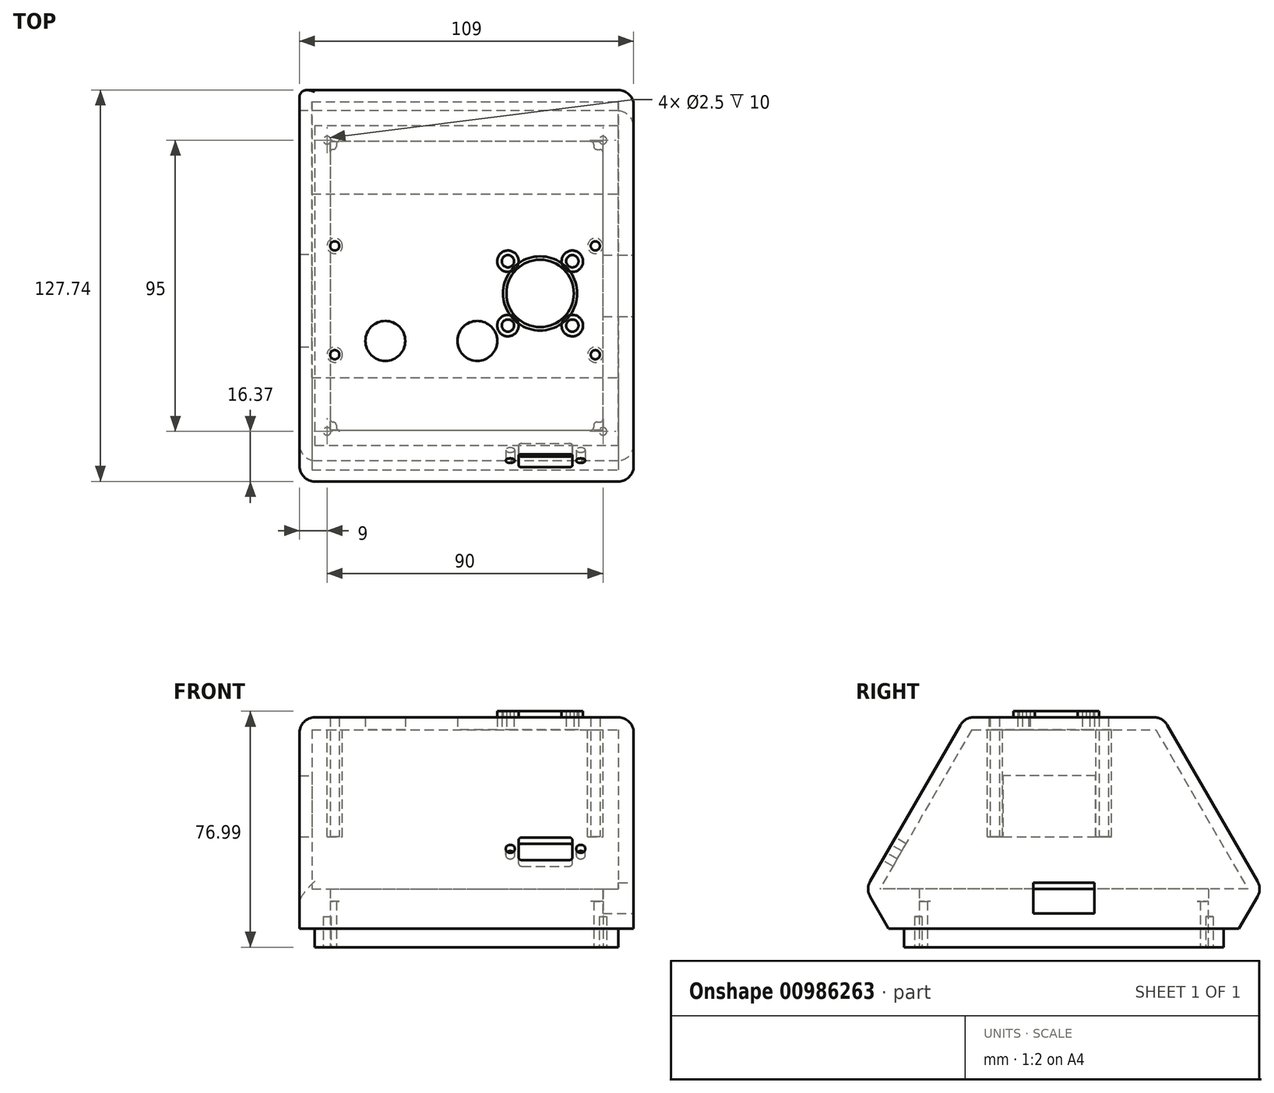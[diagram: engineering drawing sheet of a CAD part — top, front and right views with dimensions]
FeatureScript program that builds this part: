
annotation { "Feature Type Name" : "Feature", "Feature Type Description" : "" }
export const myFeature = defineFeature(function(context is Context, id is Id, definition is map)
    precondition{}
    {
        {
            var Q0;
            Q0=qCreatedBy(makeId("Top.planeOp"),FACE);
            var sketch = newSketch(context, id + "F0", { "sketchPlane" : qUnion([Q0])});
            skLineSegment(sketch, "E0.bottom", {"start": v(-50, -30) * mm, "end": v(50, -30) * mm});
            skLineSegment(sketch, "E0.top", {"start": v(-50, 30) * mm, "end": v(50, 30) * mm});
            skLineSegment(sketch, "E0.left", {"start": v(-50, -30) * mm, "end": v(-50, 30) * mm});
            skLineSegment(sketch, "E0.right", {"start": v(50, -30) * mm, "end": v(50, 30) * mm});
            skPoint(sketch, "E0.middle", {"position": v(0, 0) * mm});
            skLineSegment(sketch, "E1.bottom", {"start": v(0, -30) * mm, "end": v(0, -30) * mm});
            skLineSegment(sketch, "E1.top", {"start": v(0, 90) * mm, "end": v(0, 90) * mm});
            skLineSegment(sketch, "E1.left", {"start": v(0, -30) * mm, "end": v(0, 90) * mm, "construction": true});
            skLineSegment(sketch, "E1.right", {"start": v(0, -30) * mm, "end": v(0, 90) * mm, "construction": true});
            skPoint(sketch, "E1.middle", {"position": v(0, 30) * mm});
            skCircle(sketch, "E2", {"center": v(42.5, -22.5) * mm, "radius": 1.5 * mm});
            skCircle(sketch, "E3", {"center": v(42.5, 13) * mm, "radius": 1.5 * mm});
            skCircle(sketch, "E4.MirrorC", {"center": v(-42.5, 13) * mm, "radius": 1.5 * mm});
            skCircle(sketch, "E5.MirrorC", {"center": v(-42.5, -22.5) * mm, "radius": 1.5 * mm});
            skLineSegment(sketch, "E6.bottom", {"start": v(35, -13) * mm, "end": v(14, -13) * mm, "construction": true});
            skLineSegment(sketch, "E6.top", {"start": v(35, 8) * mm, "end": v(14, 8) * mm, "construction": true});
            skLineSegment(sketch, "E6.left", {"start": v(35, -13) * mm, "end": v(35, 8) * mm, "construction": true});
            skLineSegment(sketch, "E6.right", {"start": v(14, -13) * mm, "end": v(14, 8) * mm, "construction": true});
            skPoint(sketch, "E6.middle", {"position": v(24.5, -2.5) * mm});
            skCircle(sketch, "E7", {"center": v(14, 8) * mm, "radius": 2 * mm});
            skCircle(sketch, "E8", {"center": v(35, 8) * mm, "radius": 2 * mm});
            skCircle(sketch, "E9", {"center": v(14, -13) * mm, "radius": 2 * mm});
            skCircle(sketch, "E10", {"center": v(35, -13) * mm, "radius": 2 * mm});
            skCircle(sketch, "E11", {"center": v(24.5, -2.5) * mm, "radius": 11 * mm});
            skCircle(sketch, "E12", {"center": v(4, -18) * mm, "radius": 6.5 * mm});
            skCircle(sketch, "E13", {"center": v(-26, -18) * mm, "radius": 6.5 * mm});
            skSolve(sketch);
        }
        {
            var Q0;
            Q0=makeQuery(id+"F0.imprint","IMPRINT",FACE,{"disambiguationData":[TD([[makeQuery(id+"F0.imprint","IMPRINT",EDGE,{"derivedFrom":sQuery(id+"F0.wireOp",EDGE,"E0.bottom")}),1.0]])]});
            extrude(context, id + "F1", {"entities" : qUnion([Q0]), "depth" : 4 * mm, "offsetDistance" : 25 * mm});
        }
        {
            var Q0;
            Q0=makeQuery(id+"F1.opExtrude","CAP_FACE",FACE,{"disambiguationData":[OSD([sQuery(id+"F0.wireOp",EDGE,"E0.bottom"),sQuery(id+"F0.wireOp",EDGE,"E0.top"),sQuery(id+"F0.wireOp",EDGE,"E0.left"),sQuery(id+"F0.wireOp",EDGE,"E0.right"),sQuery(id+"F0.wireOp",EDGE,"E2"),sQuery(id+"F0.wireOp",EDGE,"E3"),sQuery(id+"F0.wireOp",EDGE,"E4.MirrorC"),sQuery(id+"F0.wireOp",EDGE,"E5.MirrorC"),sQuery(id+"F0.wireOp",EDGE,"E7"),sQuery(id+"F0.wireOp",EDGE,"E8"),sQuery(id+"F0.wireOp",EDGE,"E9"),sQuery(id+"F0.wireOp",EDGE,"E10"),sQuery(id+"F0.wireOp",EDGE,"E11"),sQuery(id+"F0.wireOp",EDGE,"E12"),sQuery(id+"F0.wireOp",EDGE,"E13")])],"isStart":true});
            var sketch = newSketch(context, id + "F2", { "sketchPlane" : qUnion([Q0])});
            skCircle(sketch, "E14", {"center": v(-42.5, 22.5) * mm, "radius": 2.5 * mm});
            skCircle(sketch, "E15", {"center": v(-42.5, -13) * mm, "radius": 2.5 * mm});
            skCircle(sketch, "E16", {"center": v(42.5, -13) * mm, "radius": 2.5 * mm});
            skCircle(sketch, "E17", {"center": v(42.5, 22.5) * mm, "radius": 2.5 * mm});
            skSolve(sketch);
        }
        {
            var Q0;
            Q0=makeQuery(id+"F2.imprint","IMPRINT",FACE,{"disambiguationData":[TD([[makeQuery(id+"F2.imprint","IMPRINT",EDGE,{"derivedFrom":sQuery(id+"F2.wireOp",EDGE,"E14")}),1.0]])]});
            var Q1;
            Q1=makeQuery(id+"F2.imprint","IMPRINT",FACE,{"disambiguationData":[TD([[makeQuery(id+"F2.imprint","IMPRINT",EDGE,{"derivedFrom":sQuery(id+"F2.wireOp",EDGE,"E15")}),1.0]])]});
            var Q2;
            Q2=makeQuery(id+"F2.imprint","IMPRINT",FACE,{"disambiguationData":[TD([[makeQuery(id+"F2.imprint","IMPRINT",EDGE,{"derivedFrom":sQuery(id+"F2.wireOp",EDGE,"E16")}),1.0]])]});
            var Q3;
            Q3=makeQuery(id+"F2.imprint","IMPRINT",FACE,{"disambiguationData":[TD([[makeQuery(id+"F2.imprint","IMPRINT",EDGE,{"derivedFrom":sQuery(id+"F2.wireOp",EDGE,"E17")}),1.0]])]});
            extrude(context, id + "F3", {"entities" : qUnion([Q0, Q1, Q2, Q3]), "operationType" : NewBodyOperationType.ADD, "depth" : 35 * mm, "offsetDistance" : 25 * mm});
        }
        {
            var Q0;
            Q0=makeQuery(id+"F1.opExtrude","CAP_FACE",FACE,{"disambiguationData":[OSD([sQuery(id+"F0.wireOp",EDGE,"E0.bottom"),sQuery(id+"F0.wireOp",EDGE,"E0.top"),sQuery(id+"F0.wireOp",EDGE,"E0.left"),sQuery(id+"F0.wireOp",EDGE,"E0.right"),sQuery(id+"F0.wireOp",EDGE,"E2"),sQuery(id+"F0.wireOp",EDGE,"E3"),sQuery(id+"F0.wireOp",EDGE,"E4.MirrorC"),sQuery(id+"F0.wireOp",EDGE,"E5.MirrorC"),sQuery(id+"F0.wireOp",EDGE,"E7"),sQuery(id+"F0.wireOp",EDGE,"E8"),sQuery(id+"F0.wireOp",EDGE,"E9"),sQuery(id+"F0.wireOp",EDGE,"E10"),sQuery(id+"F0.wireOp",EDGE,"E11"),sQuery(id+"F0.wireOp",EDGE,"E12"),sQuery(id+"F0.wireOp",EDGE,"E13")])],"isStart":false});
            var sketch = newSketch(context, id + "F4", { "sketchPlane" : qUnion([Q0])});
            skCircle(sketch, "E18", {"center": v(-42.5, 13) * mm, "radius": 2.5 * mm});
            skCircle(sketch, "E19", {"center": v(42.5, 13) * mm, "radius": 2.5 * mm});
            skCircle(sketch, "E20", {"center": v(-42.5, -22.5) * mm, "radius": 2.5 * mm});
            skCircle(sketch, "E21", {"center": v(42.5, -22.5) * mm, "radius": 2.5 * mm});
            skSolve(sketch);
        }
        {
            var Q0;
            Q0=makeQuery(id+"F4.imprint","IMPRINT",FACE,{"disambiguationData":[TD([[makeQuery(id+"F4.imprint","IMPRINT",EDGE,{"derivedFrom":makeQuery(id+"F1.opExtrude","CAP_EDGE",EDGE,{"disambiguationData":[OSD([sQuery(id+"F0.wireOp",EDGE,"E4.MirrorC")])],"isStart":false})}),-1.0]])]});
            var Q1;
            Q1=makeQuery(id+"F4.imprint","IMPRINT",FACE,{"disambiguationData":[TD([[makeQuery(id+"F4.imprint","IMPRINT",EDGE,{"derivedFrom":makeQuery(id+"F1.opExtrude","CAP_EDGE",EDGE,{"disambiguationData":[OSD([sQuery(id+"F0.wireOp",EDGE,"E3")])],"isStart":false})}),1.0]])]});
            var Q2;
            Q2=makeQuery(id+"F4.imprint","IMPRINT",FACE,{"disambiguationData":[TD([[makeQuery(id+"F4.imprint","IMPRINT",EDGE,{"derivedFrom":makeQuery(id+"F1.opExtrude","CAP_EDGE",EDGE,{"disambiguationData":[OSD([sQuery(id+"F0.wireOp",EDGE,"E2")])],"isStart":false})}),1.0]])]});
            var Q3;
            Q3=makeQuery(id+"F4.imprint","IMPRINT",FACE,{"disambiguationData":[TD([[makeQuery(id+"F4.imprint","IMPRINT",EDGE,{"derivedFrom":makeQuery(id+"F1.opExtrude","CAP_EDGE",EDGE,{"disambiguationData":[OSD([sQuery(id+"F0.wireOp",EDGE,"E5.MirrorC")])],"isStart":false})}),-1.0]])]});
            extrude(context, id + "F5", {"entities" : qUnion([Q0, Q1, Q2, Q3]), "operationType" : NewBodyOperationType.ADD, "oppositeDirection" : true, "depth" : 25 * mm, "offsetDistance" : 25 * mm});
        }
        {
            var Q0;
            Q0=makeQuery(id+"F1.opExtrude","SWEPT_FACE",FACE,{"disambiguationData":[OSD([sQuery(id+"F0.wireOp",EDGE,"E0.right")])]});
            var sketch = newSketch(context, id + "F6", { "sketchPlane" : qUnion([Q0])});
            skLineSegment(sketch, "E22", {"start": v(-30, 0) * mm, "end": v(-57.5, -47.63) * mm});
            skLineSegment(sketch, "E23", {"start": v(-30, 0) * mm, "end": v(-28, 0) * mm});
            skLineSegment(sketch, "E24", {"start": v(-28, 0) * mm, "end": v(-28, 4) * mm});
            skLineSegment(sketch, "E25", {"start": v(-28, 4) * mm, "end": v(-30, 4) * mm});
            skLineSegment(sketch, "E26.0", {"start": v(-33.46, 2) * mm, "end": v(-60.96, -45.63) * mm});
            skLineSegment(sketch, "E27", {"start": v(-33.46, 2) * mm, "end": v(-32.3, 4) * mm});
            skLineSegment(sketch, "E28", {"start": v(-30, 4) * mm, "end": v(-32.3, 4) * mm});
            skLineSegment(sketch, "E29", {"start": v(0, 4) * mm, "end": v(0, -52) * mm, "construction": true});
            skLineSegment(sketch, "E30", {"start": v(0, -52) * mm, "end": v(-69.6, -52) * mm, "construction": true});
            skLineSegment(sketch, "E31", {"start": v(-57.5, -47.63) * mm, "end": v(-60.02, -52) * mm});
            skLineSegment(sketch, "E32", {"start": v(-60.96, -45.63) * mm, "end": v(-64.64, -52) * mm});
            skLineSegment(sketch, "E33", {"start": v(-60.02, -52) * mm, "end": v(-64.64, -52) * mm});
            skLineSegment(sketch, "E34.MirrorCS", {"start": v(28, 0) * mm, "end": v(28, 4) * mm});
            skLineSegment(sketch, "E35.MirrorCS", {"start": v(28, 4) * mm, "end": v(30, 4) * mm});
            skLineSegment(sketch, "E36.MirrorCS", {"start": v(30, 4) * mm, "end": v(32.3, 4) * mm});
            skLineSegment(sketch, "E37.MirrorCS", {"start": v(33.46, 2) * mm, "end": v(32.3, 4) * mm});
            skLineSegment(sketch, "E38.MirrorCS", {"start": v(33.46, 2) * mm, "end": v(60.96, -45.63) * mm});
            skLineSegment(sketch, "E39.MirrorCS", {"start": v(30, 0) * mm, "end": v(28, 0) * mm});
            skLineSegment(sketch, "E40.MirrorCS", {"start": v(30, 0) * mm, "end": v(57.5, -47.63) * mm});
            skLineSegment(sketch, "E41.MirrorCS", {"start": v(57.5, -47.63) * mm, "end": v(60.02, -52) * mm});
            skLineSegment(sketch, "E42.MirrorCS", {"start": v(60.96, -45.63) * mm, "end": v(64.64, -52) * mm});
            skLineSegment(sketch, "E43", {"start": v(64.64, -52) * mm, "end": v(60.02, -52) * mm});
            skSolve(sketch);
        }
        {
            var Q0;
            Q0=makeQuery(id+"F6.imprint","IMPRINT",FACE,{"disambiguationData":[TD([[makeQuery(id+"F6.imprint","IMPRINT",EDGE,{"derivedFrom":sQuery(id+"F6.wireOp",EDGE,"E23")}),1.0]])]});
            var Q1;
            Q1=makeQuery(id+"F6.imprint","IMPRINT",FACE,{"disambiguationData":[TD([[makeQuery(id+"F6.imprint","IMPRINT",EDGE,{"derivedFrom":sQuery(id+"F6.wireOp",EDGE,"E22")}),-1.0]])]});
            var Q2;
            Q2=makeQuery(id+"F6.imprint","IMPRINT",FACE,{"disambiguationData":[TD([[makeQuery(id+"F6.imprint","IMPRINT",EDGE,{"derivedFrom":sQuery(id+"F6.wireOp",EDGE,"E34.MirrorCS")}),-1.0]])]});
            var Q3;
            Q3=makeQuery(id+"F6.imprint","IMPRINT",FACE,{"disambiguationData":[TD([[makeQuery(id+"F6.imprint","IMPRINT",EDGE,{"derivedFrom":sQuery(id+"F6.wireOp",EDGE,"E36.MirrorCS")}),-1.0]])]});
            extrude(context, id + "F7", {"entities" : qUnion([Q0, Q1, Q2, Q3]), "operationType" : NewBodyOperationType.ADD, "oppositeDirection" : true, "depth" : 100 * mm, "offsetDistance" : 25 * mm});
        }
        {
            var Q0;
            Q0=makeQuery(id+"F7.boolean.opBoolean","MERGE",FACE,{"derivedFrom":[makeQuery(id+"F1.opExtrude","SWEPT_FACE",FACE,{"disambiguationData":[OSD([sQuery(id+"F0.wireOp",EDGE,"E0.right")])]}),makeQuery(id+"F7.opExtrude","CAP_FACE",FACE,{"disambiguationData":[OSD([sQuery(id+"F6.wireOp",EDGE,"E22"),sQuery(id+"F6.wireOp",EDGE,"E23"),sQuery(id+"F6.wireOp",EDGE,"E24"),sQuery(id+"F6.wireOp",EDGE,"E25"),sQuery(id+"F6.wireOp",EDGE,"E26.0"),sQuery(id+"F6.wireOp",EDGE,"E27"),sQuery(id+"F6.wireOp",EDGE,"E28"),sQuery(id+"F6.wireOp",EDGE,"E31"),sQuery(id+"F6.wireOp",EDGE,"E32"),sQuery(id+"F6.wireOp",EDGE,"E33")])],"isStart":true}),makeQuery(id+"F7.opExtrude","CAP_FACE",FACE,{"disambiguationData":[OSD([sQuery(id+"F6.wireOp",EDGE,"E34.MirrorCS"),sQuery(id+"F6.wireOp",EDGE,"E35.MirrorCS"),sQuery(id+"F6.wireOp",EDGE,"E36.MirrorCS"),sQuery(id+"F6.wireOp",EDGE,"E37.MirrorCS"),sQuery(id+"F6.wireOp",EDGE,"E38.MirrorCS"),sQuery(id+"F6.wireOp",EDGE,"E39.MirrorCS"),sQuery(id+"F6.wireOp",EDGE,"E40.MirrorCS"),sQuery(id+"F6.wireOp",EDGE,"E41.MirrorCS"),sQuery(id+"F6.wireOp",EDGE,"E42.MirrorCS"),sQuery(id+"F6.wireOp",EDGE,"E43")])],"isStart":true})]});
            var sketch = newSketch(context, id + "F8", { "sketchPlane" : qUnion([Q0])});
            skLineSegment(sketch, "E44", {"start": v(-64.64, -52) * mm, "end": v(64.64, -52) * mm});
            skLineSegment(sketch, "E45", {"start": v(64.64, -52) * mm, "end": v(32.3, 4) * mm});
            skLineSegment(sketch, "E46", {"start": v(32.3, 4) * mm, "end": v(-32.3, 4) * mm});
            skLineSegment(sketch, "E47", {"start": v(-32.3, 4) * mm, "end": v(-64.64, -52) * mm});
            skSolve(sketch);
        }
        {
            var Q0;
            Q0 = qSketchRegion(id + "F8", true);
            extrude(context, id + "F9", {"entities" : qUnion([Q0]), "operationType" : NewBodyOperationType.ADD, "depth" : 5 * mm, "offsetDistance" : 25 * mm});
        }
        {
            var Q0;
            Q0=makeQuery(id+"F7.boolean.opBoolean","MERGE",FACE,{"derivedFrom":[makeQuery(id+"F1.opExtrude","SWEPT_FACE",FACE,{"disambiguationData":[OSD([sQuery(id+"F0.wireOp",EDGE,"E0.left")])]}),makeQuery(id+"F7.opExtrude","CAP_FACE",FACE,{"disambiguationData":[OSD([sQuery(id+"F6.wireOp",EDGE,"E22"),sQuery(id+"F6.wireOp",EDGE,"E23"),sQuery(id+"F6.wireOp",EDGE,"E24"),sQuery(id+"F6.wireOp",EDGE,"E25"),sQuery(id+"F6.wireOp",EDGE,"E26.0"),sQuery(id+"F6.wireOp",EDGE,"E27"),sQuery(id+"F6.wireOp",EDGE,"E28"),sQuery(id+"F6.wireOp",EDGE,"E31"),sQuery(id+"F6.wireOp",EDGE,"E32"),sQuery(id+"F6.wireOp",EDGE,"E33")])],"isStart":false}),makeQuery(id+"F7.opExtrude","CAP_FACE",FACE,{"disambiguationData":[OSD([sQuery(id+"F6.wireOp",EDGE,"E34.MirrorCS"),sQuery(id+"F6.wireOp",EDGE,"E35.MirrorCS"),sQuery(id+"F6.wireOp",EDGE,"E36.MirrorCS"),sQuery(id+"F6.wireOp",EDGE,"E37.MirrorCS"),sQuery(id+"F6.wireOp",EDGE,"E38.MirrorCS"),sQuery(id+"F6.wireOp",EDGE,"E39.MirrorCS"),sQuery(id+"F6.wireOp",EDGE,"E40.MirrorCS"),sQuery(id+"F6.wireOp",EDGE,"E41.MirrorCS"),sQuery(id+"F6.wireOp",EDGE,"E42.MirrorCS"),sQuery(id+"F6.wireOp",EDGE,"E43")])],"isStart":false})]});
            var sketch = newSketch(context, id + "F10", { "sketchPlane" : qUnion([Q0])});
            skLineSegment(sketch, "E48", {"start": v(-64.64, -52) * mm, "end": v(64.64, -52) * mm});
            skLineSegment(sketch, "E49", {"start": v(64.64, -52) * mm, "end": v(32.3, 4) * mm});
            skLineSegment(sketch, "E50", {"start": v(32.3, 4) * mm, "end": v(-32.3, 4) * mm});
            skLineSegment(sketch, "E51", {"start": v(-32.3, 4) * mm, "end": v(-64.64, -52) * mm});
            skLineSegment(sketch, "E52", {"start": v(19.9, -35.02) * mm, "end": v(-10.31, -35.02) * mm});
            skLineSegment(sketch, "E53", {"start": v(-10.31, -35.02) * mm, "end": v(-10.31, -15.02) * mm});
            skLineSegment(sketch, "E54", {"start": v(-10.31, -15.02) * mm, "end": v(19.9, -15.02) * mm});
            skLineSegment(sketch, "E55", {"start": v(19.9, -15.02) * mm, "end": v(19.9, -35.02) * mm});
            skSolve(sketch);
        }
        {
            var Q0;
            Q0 = qSketchRegion(id + "F10", true);
            extrude(context, id + "F11", {"entities" : qUnion([Q0]), "operationType" : NewBodyOperationType.ADD, "depth" : 4 * mm, "offsetDistance" : 25 * mm});
        }
        {
            var Q0;
            Q0=makeQuery(id+"F11.opExtrude","CAP_FACE",FACE,{"disambiguationData":[OSD([sQuery(id+"F10.wireOp",EDGE,"E48"),sQuery(id+"F10.wireOp",EDGE,"E49"),sQuery(id+"F10.wireOp",EDGE,"E50"),sQuery(id+"F10.wireOp",EDGE,"E51"),sQuery(id+"F10.wireOp",EDGE,"E52"),sQuery(id+"F10.wireOp",EDGE,"E53"),sQuery(id+"F10.wireOp",EDGE,"E54"),sQuery(id+"F10.wireOp",EDGE,"E55")])],"isStart":false});
            var sketch = newSketch(context, id + "F12", { "sketchPlane" : qUnion([Q0])});
            skLineSegment(sketch, "E56", {"start": v(-64.64, -52) * mm, "end": v(-57.14, -65) * mm});
            skLineSegment(sketch, "E57", {"start": v(64.64, -52) * mm, "end": v(57.14, -65) * mm});
            skLineSegment(sketch, "E58", {"start": v(-57.14, -65) * mm, "end": v(57.14, -65) * mm});
            skLineSegment(sketch, "E59", {"start": v(64.64, -52) * mm, "end": v(-63, -52) * mm});
            skSolve(sketch);
        }
        {
            var Q0;
            {var subQ1=sQuery(id+"F12.wireOp",EDGE,"E56");Q0=makeQuery(id+"F12.imprint","IMPRINT",FACE,{"disambiguationData":[TD([[makeQuery(id+"F12.imprint","IMPRINT",EDGE,{"derivedFrom":subQ1}),1.0]])]});}
            var Q1;
            Q1=makeQuery(id+"F9.opExtrude","CAP_FACE",FACE,{"disambiguationData":[OSD([sQuery(id+"F8.wireOp",EDGE,"E44"),sQuery(id+"F8.wireOp",EDGE,"E45"),sQuery(id+"F8.wireOp",EDGE,"E46"),sQuery(id+"F8.wireOp",EDGE,"E47")])],"isStart":false});
            extrude(context, id + "F13", {"entities" : qUnion([Q0]), "operationType" : NewBodyOperationType.ADD, "endBound" : BoundingType.UP_TO_SURFACE, "oppositeDirection" : true, "depth" : 25 * mm, "endBoundEntityFace" : qUnion([Q1]), "offsetDistance" : 25 * mm});
        }
        {
            var Q0;
            Q0=makeQuery(id+"F13.opExtrude","SWEPT_FACE",FACE,{"disambiguationData":[OSD([sQuery(id+"F12.wireOp",EDGE,"E58")])]});
            var sketch = newSketch(context, id + "F14", { "sketchPlane" : qUnion([Q0])});
            skLineSegment(sketch, "E60", {"start": v(55, 57.14) * mm, "end": v(55, -57.14) * mm});
            skLineSegment(sketch, "E61", {"start": v(55, -57.14) * mm, "end": v(-54, -57.14) * mm});
            skLineSegment(sketch, "E62", {"start": v(-54, -57.14) * mm, "end": v(-54, 57.14) * mm});
            skLineSegment(sketch, "E63", {"start": v(-54, 57.14) * mm, "end": v(55, 57.14) * mm});
            skLineSegment(sketch, "E64.0", {"start": v(-49, 52.14) * mm, "end": v(50, 52.14) * mm});
            skLineSegment(sketch, "E64.1", {"start": v(-49, -52.14) * mm, "end": v(-49, 52.14) * mm});
            skLineSegment(sketch, "E64.2", {"start": v(50, -52.14) * mm, "end": v(-49, -52.14) * mm});
            skLineSegment(sketch, "E64.3", {"start": v(50, 52.14) * mm, "end": v(50, -52.14) * mm});
            skSolve(sketch);
        }
        {
            var Q0;
            Q0=makeQuery(id+"F14.imprint","IMPRINT",FACE,{"disambiguationData":[TD([[makeQuery(id+"F14.imprint","IMPRINT",EDGE,{"derivedFrom":sQuery(id+"F14.wireOp",EDGE,"E64.0")}),-1.0]])]});
            extrude(context, id + "F15", {"entities" : qUnion([Q0]), "operationType" : NewBodyOperationType.ADD, "depth" : 6 * mm, "offsetDistance" : 25 * mm});
        }
        {
            var Q0;
            Q0=makeQuery(id+"F11.opExtrude","CAP_EDGE",EDGE,{"disambiguationData":[OSD([sQuery(id+"F10.wireOp",EDGE,"E49")])],"isStart":false});
            var Q1;
            Q1=makeQuery(id+"F11.boolean.opBoolean","MERGE",EDGE,{"derivedFrom":[makeQuery(id+"F9.boolean.opBoolean","MERGE",EDGE,{"derivedFrom":[makeQuery(id+"F7.opExtrude","SWEPT_EDGE",EDGE,{"disambiguationData":[OSD([sQuery(id+"F6.wireOp",EDGE,"E27"),sQuery(id+"F6.wireOp",EDGE,"E28")])]}),makeQuery(id+"F9.opExtrude","SWEPT_EDGE",EDGE,{"disambiguationData":[OSD([sQuery(id+"F8.wireOp",EDGE,"E46"),sQuery(id+"F8.wireOp",EDGE,"E47")])]})]}),makeQuery(id+"F11.opExtrude","SWEPT_EDGE",EDGE,{"disambiguationData":[OSD([sQuery(id+"F10.wireOp",EDGE,"E49"),sQuery(id+"F10.wireOp",EDGE,"E50")])]})]});
            var Q2;
            Q2=makeQuery(id+"F11.opExtrude","CAP_EDGE",EDGE,{"disambiguationData":[OSD([sQuery(id+"F10.wireOp",EDGE,"E50")])],"isStart":false});
            var Q3;
            {var subQ0=sQuery(id+"F10.wireOp",EDGE,"E49");Q3=makeQuery(id+"F13.boolean.opBoolean","MERGE",EDGE,{"derivedFrom":[makeQuery(id+"F11.boolean.opBoolean","MERGE",EDGE,{"derivedFrom":[makeQuery(id+"F9.boolean.opBoolean","MERGE",EDGE,{"derivedFrom":[makeQuery(id+"F7.opExtrude","SWEPT_EDGE",EDGE,{"disambiguationData":[OSD([sQuery(id+"F6.wireOp",EDGE,"E32"),sQuery(id+"F6.wireOp",EDGE,"E33")])]}),makeQuery(id+"F9.opExtrude","SWEPT_EDGE",EDGE,{"disambiguationData":[OSD([sQuery(id+"F8.wireOp",EDGE,"E44"),sQuery(id+"F8.wireOp",EDGE,"E47")])]})]}),makeQuery(id+"F11.opExtrude","SWEPT_EDGE",EDGE,{"disambiguationData":[OSD([sQuery(id+"F10.wireOp",EDGE,"E48"),subQ0])]})]}),makeQuery(id+"F13.opExtrude","SWEPT_EDGE",EDGE,{"disambiguationData":[OSD([subQ0,sQuery(id+"F12.wireOp",EDGE,"E57"),sQuery(id+"F12.wireOp",EDGE,"E59")])]})]});}
            var Q4;
            Q4=makeQuery(id+"F13.opExtrude","CAP_EDGE",EDGE,{"disambiguationData":[OSD([sQuery(id+"F12.wireOp",EDGE,"E57")])],"isStart":true});
            var Q5;
            Q5=makeQuery(id+"F13.opExtrude","CAP_EDGE",EDGE,{"disambiguationData":[OSD([sQuery(id+"F12.wireOp",EDGE,"E57")])],"isStart":false});
            var Q6;
            Q6=makeQuery(id+"F9.opExtrude","CAP_EDGE",EDGE,{"disambiguationData":[OSD([sQuery(id+"F8.wireOp",EDGE,"E47")])],"isStart":false});
            var Q7;
            Q7=makeQuery(id+"F11.opExtrude","CAP_EDGE",EDGE,{"disambiguationData":[OSD([sQuery(id+"F10.wireOp",EDGE,"E51")])],"isStart":false});
            var Q8;
            Q8=makeQuery(id+"F11.boolean.opBoolean","MERGE",EDGE,{"derivedFrom":[makeQuery(id+"F9.boolean.opBoolean","MERGE",EDGE,{"derivedFrom":[makeQuery(id+"F7.opExtrude","SWEPT_EDGE",EDGE,{"disambiguationData":[OSD([sQuery(id+"F6.wireOp",EDGE,"E36.MirrorCS"),sQuery(id+"F6.wireOp",EDGE,"E37.MirrorCS")])]}),makeQuery(id+"F9.opExtrude","SWEPT_EDGE",EDGE,{"disambiguationData":[OSD([sQuery(id+"F8.wireOp",EDGE,"E45"),sQuery(id+"F8.wireOp",EDGE,"E46")])]})]}),makeQuery(id+"F11.opExtrude","SWEPT_EDGE",EDGE,{"disambiguationData":[OSD([sQuery(id+"F10.wireOp",EDGE,"E50"),sQuery(id+"F10.wireOp",EDGE,"E51")])]})]});
            var Q9;
            {var subQ0=sQuery(id+"F10.wireOp",EDGE,"E51");var subQ1=sQuery(id+"F10.wireOp",EDGE,"E48");Q9=makeQuery(id+"F13.boolean.opBoolean","MERGE",EDGE,{"derivedFrom":[makeQuery(id+"F11.boolean.opBoolean","MERGE",EDGE,{"derivedFrom":[makeQuery(id+"F9.boolean.opBoolean","MERGE",EDGE,{"derivedFrom":[makeQuery(id+"F7.opExtrude","SWEPT_EDGE",EDGE,{"disambiguationData":[OSD([sQuery(id+"F6.wireOp",EDGE,"E42.MirrorCS"),sQuery(id+"F6.wireOp",EDGE,"E43")])]}),makeQuery(id+"F9.opExtrude","SWEPT_EDGE",EDGE,{"disambiguationData":[OSD([sQuery(id+"F8.wireOp",EDGE,"E44"),sQuery(id+"F8.wireOp",EDGE,"E45")])]})]}),makeQuery(id+"F11.opExtrude","SWEPT_EDGE",EDGE,{"disambiguationData":[OSD([subQ1,subQ0])]})]}),makeQuery(id+"F13.opExtrude","SWEPT_EDGE",EDGE,{"disambiguationData":[OSD([subQ1,subQ0,sQuery(id+"F12.wireOp",EDGE,"E56")])]})]});}
            var Q10;
            Q10=makeQuery(id+"F13.opExtrude","CAP_EDGE",EDGE,{"disambiguationData":[OSD([sQuery(id+"F12.wireOp",EDGE,"E56")])],"isStart":false});
            var Q11;
            Q11=makeQuery(id+"F9.opExtrude","CAP_EDGE",EDGE,{"disambiguationData":[OSD([sQuery(id+"F8.wireOp",EDGE,"E45")])],"isStart":false});
            var Q12;
            Q12=makeQuery(id+"F9.opExtrude","CAP_EDGE",EDGE,{"disambiguationData":[OSD([sQuery(id+"F8.wireOp",EDGE,"E46")])],"isStart":false});
            fillet(context, id + "F16", {"entities" : qUnion([Q0, Q1, Q2, Q3, Q4, Q5, Q6, Q7, Q8, Q9, Q10, Q11, Q12]), "radius" : 5 * mm, "tangentPropagation" : true, "allowEdgeOverflow" : false});
        }
        {
            var Q0;
            Q0=makeQuery(id+"F15.opExtrude","CAP_FACE",FACE,{"disambiguationData":[OSD([sQuery(id+"F14.wireOp",EDGE,"E64.0"),sQuery(id+"F14.wireOp",EDGE,"E64.1"),sQuery(id+"F14.wireOp",EDGE,"E64.2"),sQuery(id+"F14.wireOp",EDGE,"E64.3")])],"isStart":false});
            var sketch = newSketch(context, id + "F17", { "sketchPlane" : qUnion([Q0])});
            skLineSegment(sketch, "E65.0", {"start": v(-44, 47.14) * mm, "end": v(45, 47.14) * mm});
            skLineSegment(sketch, "E65.1", {"start": v(-44, -47.14) * mm, "end": v(-44, 47.14) * mm});
            skLineSegment(sketch, "E65.2", {"start": v(45, -47.14) * mm, "end": v(-44, -47.14) * mm});
            skLineSegment(sketch, "E65.3", {"start": v(45, 47.14) * mm, "end": v(45, -47.14) * mm});
            skSolve(sketch);
        }
        {
            var Q0;
            Q0=makeQuery(id+"F17.imprint","IMPRINT",FACE,{"disambiguationData":[TD([[makeQuery(id+"F17.imprint","IMPRINT",EDGE,{"derivedFrom":sQuery(id+"F17.wireOp",EDGE,"E65.0")}),-1.0]])]});
            extrude(context, id + "F18", {"entities" : qUnion([Q0]), "operationType" : NewBodyOperationType.REMOVE, "oppositeDirection" : true, "depth" : 25 * mm, "offsetDistance" : 25 * mm});
        }
        {
            var Q0;
            Q0=makeQuery(id+"F13.boolean.opBoolean","MERGE",FACE,{"derivedFrom":[makeQuery(id+"F9.opExtrude","CAP_FACE",FACE,{"disambiguationData":[OSD([sQuery(id+"F8.wireOp",EDGE,"E44"),sQuery(id+"F8.wireOp",EDGE,"E45"),sQuery(id+"F8.wireOp",EDGE,"E46"),sQuery(id+"F8.wireOp",EDGE,"E47")])],"isStart":false}),makeQuery(id+"F13.opExtrude","CAP_FACE",FACE,{"disambiguationData":[OSD([sQuery(id+"F10.wireOp",EDGE,"E48"),sQuery(id+"F12.wireOp",EDGE,"E56"),sQuery(id+"F12.wireOp",EDGE,"E57"),sQuery(id+"F12.wireOp",EDGE,"E58"),sQuery(id+"F12.wireOp",EDGE,"E59")])],"isStart":false})]});
            var sketch = newSketch(context, id + "F19", { "sketchPlane" : qUnion([Q0])});
            skLineSegment(sketch, "E66.bottom", {"start": v(-10, -60) * mm, "end": v(10, -60) * mm});
            skLineSegment(sketch, "E66.top", {"start": v(-10, -50) * mm, "end": v(10, -50) * mm});
            skLineSegment(sketch, "E66.left", {"start": v(-10, -60) * mm, "end": v(-10, -50) * mm});
            skLineSegment(sketch, "E66.right", {"start": v(10, -60) * mm, "end": v(10, -50) * mm});
            skPoint(sketch, "E66.middle", {"position": v(0, -55) * mm});
            skSolve(sketch);
        }
        {
            var Q0;
            Q0=makeQuery(id+"F19.imprint","IMPRINT",FACE,{"disambiguationData":[TD([[makeQuery(id+"F19.imprint","IMPRINT",EDGE,{"derivedFrom":sQuery(id+"F19.wireOp",EDGE,"E66.bottom")}),1.0]])]});
            extrude(context, id + "F20", {"entities" : qUnion([Q0]), "operationType" : NewBodyOperationType.REMOVE, "oppositeDirection" : true, "depth" : 10 * mm, "offsetDistance" : 25 * mm});
        }
        {
            var Q0;
            Q0=makeQuery(id+"F15.opExtrude","CAP_FACE",FACE,{"disambiguationData":[OSD([sQuery(id+"F14.wireOp",EDGE,"E64.0"),sQuery(id+"F14.wireOp",EDGE,"E64.1"),sQuery(id+"F14.wireOp",EDGE,"E64.2"),sQuery(id+"F14.wireOp",EDGE,"E64.3")])],"isStart":false});
            var sketch = newSketch(context, id + "F21", { "sketchPlane" : qUnion([Q0])});
            skLineSegment(sketch, "E67.bottom", {"start": v(-45, -47.5) * mm, "end": v(45, -47.5) * mm});
            skLineSegment(sketch, "E67.top", {"start": v(-45, 47.5) * mm, "end": v(45, 47.5) * mm});
            skLineSegment(sketch, "E67.left", {"start": v(-45, -47.5) * mm, "end": v(-45, 47.5) * mm});
            skLineSegment(sketch, "E67.right", {"start": v(45, -47.5) * mm, "end": v(45, 47.5) * mm});
            skPoint(sketch, "E67.middle", {"position": v(0, 0) * mm});
            skLineSegment(sketch, "E68.bottom", {"start": v(-42, 44.5) * mm, "end": v(-48, 44.5) * mm});
            skLineSegment(sketch, "E68.top", {"start": v(-42, 50.5) * mm, "end": v(-48, 50.5) * mm});
            skLineSegment(sketch, "E68.left", {"start": v(-42, 44.5) * mm, "end": v(-42, 50.5) * mm});
            skLineSegment(sketch, "E68.right", {"start": v(-48, 44.5) * mm, "end": v(-48, 50.5) * mm});
            skPoint(sketch, "E68.middle", {"position": v(-45, 47.5) * mm});
            skLineSegment(sketch, "E69.bottom", {"start": v(-48, -50.5) * mm, "end": v(-42, -50.5) * mm});
            skLineSegment(sketch, "E69.top", {"start": v(-48, -44.5) * mm, "end": v(-42, -44.5) * mm});
            skLineSegment(sketch, "E69.left", {"start": v(-48, -50.5) * mm, "end": v(-48, -44.5) * mm});
            skLineSegment(sketch, "E69.right", {"start": v(-42, -50.5) * mm, "end": v(-42, -44.5) * mm});
            skPoint(sketch, "E69.middle", {"position": v(-45, -47.5) * mm});
            skLineSegment(sketch, "E70.bottom", {"start": v(42, -50.5) * mm, "end": v(48, -50.5) * mm});
            skLineSegment(sketch, "E70.top", {"start": v(42, -44.5) * mm, "end": v(48, -44.5) * mm});
            skLineSegment(sketch, "E70.left", {"start": v(42, -50.5) * mm, "end": v(42, -44.5) * mm});
            skLineSegment(sketch, "E70.right", {"start": v(48, -50.5) * mm, "end": v(48, -44.5) * mm});
            skPoint(sketch, "E70.middle", {"position": v(45, -47.5) * mm});
            skLineSegment(sketch, "E71.bottom", {"start": v(42, 44.5) * mm, "end": v(48, 44.5) * mm});
            skLineSegment(sketch, "E71.top", {"start": v(42, 50.5) * mm, "end": v(48, 50.5) * mm});
            skLineSegment(sketch, "E71.left", {"start": v(42, 44.5) * mm, "end": v(42, 50.5) * mm});
            skLineSegment(sketch, "E71.right", {"start": v(48, 44.5) * mm, "end": v(48, 50.5) * mm});
            skPoint(sketch, "E71.middle", {"position": v(45, 47.5) * mm});
            skSolve(sketch);
        }
        {
            var Q0;
            {var subQ4=sQuery(id+"F21.wireOp",EDGE,"E69.bottom");Q0=makeQuery(id+"F21.imprint","IMPRINT",FACE,{"disambiguationData":[TD([[makeQuery(id+"F21.imprint","IMPRINT",EDGE,{"derivedFrom":subQ4}),1.0]])]});}
            var Q1;
            {var subQ0=sQuery(id+"F21.wireOp",EDGE,"E69.right");var subQ1=sQuery(id+"F21.wireOp",EDGE,"E69.top");var subQ2=makeQuery(id+"F21.imprint","INTERSECT",VERTEX,{"derivedFrom":[subQ1,subQ0]});Q1=makeQuery(id+"F21.imprint","IMPRINT",FACE,{"disambiguationData":[TD([[makeQuery(id+"F21.imprint","IMPRINT",EDGE,{"disambiguationData":[TD([[subQ2,1.0]])],"derivedFrom":subQ1}),-1.0]])]});}
            var Q2;
            {var subQ1=sQuery(id+"F21.wireOp",EDGE,"E67.bottom");var subQ5=sQuery(id+"F21.wireOp",EDGE,"E67.left");var subQ6=makeQuery(id+"F21.imprint","INTERSECT",VERTEX,{"derivedFrom":[subQ1,subQ5]});Q2=makeQuery(id+"F21.imprint","IMPRINT",FACE,{"disambiguationData":[TD([[makeQuery(id+"F21.imprint","IMPRINT",EDGE,{"disambiguationData":[TD([[subQ6,-1.0]])],"derivedFrom":subQ1}),1.0]])]});}
            var Q3;
            {var subQ0=sQuery(id+"F21.wireOp",EDGE,"E67.right");var subQ3=sQuery(id+"F21.wireOp",EDGE,"E70.top");var subQ4=makeQuery(id+"F21.imprint","INTERSECT",VERTEX,{"derivedFrom":[subQ0,subQ3]});Q3=makeQuery(id+"F21.imprint","IMPRINT",FACE,{"disambiguationData":[TD([[makeQuery(id+"F21.imprint","IMPRINT",EDGE,{"disambiguationData":[TD([[subQ4,-1.0]])],"derivedFrom":subQ0}),-1.0]])]});}
            var Q4;
            {var subQ0=sQuery(id+"F21.wireOp",EDGE,"E70.bottom");Q4=makeQuery(id+"F21.imprint","IMPRINT",FACE,{"disambiguationData":[TD([[makeQuery(id+"F21.imprint","IMPRINT",EDGE,{"derivedFrom":subQ0}),1.0]])]});}
            var Q5;
            {var subQ0=sQuery(id+"F21.wireOp",EDGE,"E67.right");var subQ1=sQuery(id+"F21.wireOp",EDGE,"E67.bottom");var subQ2=makeQuery(id+"F21.imprint","INTERSECT",VERTEX,{"derivedFrom":[subQ1,subQ0]});Q5=makeQuery(id+"F21.imprint","IMPRINT",FACE,{"disambiguationData":[TD([[makeQuery(id+"F21.imprint","IMPRINT",EDGE,{"disambiguationData":[TD([[subQ2,1.0]])],"derivedFrom":subQ1}),1.0]])]});}
            var Q6;
            {var subQ0=sQuery(id+"F21.wireOp",EDGE,"E67.right");var subQ1=sQuery(id+"F21.wireOp",EDGE,"E67.top");var subQ2=makeQuery(id+"F21.imprint","INTERSECT",VERTEX,{"derivedFrom":[subQ1,subQ0]});Q6=makeQuery(id+"F21.imprint","IMPRINT",FACE,{"disambiguationData":[TD([[makeQuery(id+"F21.imprint","IMPRINT",EDGE,{"disambiguationData":[TD([[subQ2,1.0]])],"derivedFrom":subQ1}),-1.0]])]});}
            var Q7;
            {var subQ0=sQuery(id+"F21.wireOp",EDGE,"E67.right");var subQ3=sQuery(id+"F21.wireOp",EDGE,"E71.bottom");var subQ4=makeQuery(id+"F21.imprint","INTERSECT",VERTEX,{"derivedFrom":[subQ0,subQ3]});Q7=makeQuery(id+"F21.imprint","IMPRINT",FACE,{"disambiguationData":[TD([[makeQuery(id+"F21.imprint","IMPRINT",EDGE,{"disambiguationData":[TD([[subQ4,1.0]])],"derivedFrom":subQ0}),-1.0]])]});}
            var Q8;
            {var subQ9=sQuery(id+"F21.wireOp",EDGE,"E71.top");Q8=makeQuery(id+"F21.imprint","IMPRINT",FACE,{"disambiguationData":[TD([[makeQuery(id+"F21.imprint","IMPRINT",EDGE,{"derivedFrom":subQ9}),-1.0]])]});}
            var Q9;
            {var subQ0=sQuery(id+"F21.wireOp",EDGE,"E68.left");var subQ1=sQuery(id+"F21.wireOp",EDGE,"E68.bottom");var subQ2=makeQuery(id+"F21.imprint","INTERSECT",VERTEX,{"derivedFrom":[subQ1,subQ0]});Q9=makeQuery(id+"F21.imprint","IMPRINT",FACE,{"disambiguationData":[TD([[makeQuery(id+"F21.imprint","IMPRINT",EDGE,{"disambiguationData":[TD([[subQ2,-1.0]])],"derivedFrom":subQ1}),-1.0]])]});}
            var Q10;
            {var subQ1=sQuery(id+"F21.wireOp",EDGE,"E67.top");var subQ5=sQuery(id+"F21.wireOp",EDGE,"E67.left");var subQ6=makeQuery(id+"F21.imprint","INTERSECT",VERTEX,{"derivedFrom":[subQ1,subQ5]});Q10=makeQuery(id+"F21.imprint","IMPRINT",FACE,{"disambiguationData":[TD([[makeQuery(id+"F21.imprint","IMPRINT",EDGE,{"disambiguationData":[TD([[subQ6,-1.0]])],"derivedFrom":subQ1}),-1.0]])]});}
            var Q11;
            {var subQ0=sQuery(id+"F21.wireOp",EDGE,"E68.top");Q11=makeQuery(id+"F21.imprint","IMPRINT",FACE,{"disambiguationData":[TD([[makeQuery(id+"F21.imprint","IMPRINT",EDGE,{"derivedFrom":subQ0}),1.0]])]});}
            extrude(context, id + "F22", {"entities" : qUnion([Q0, Q1, Q2, Q3, Q4, Q5, Q6, Q7, Q8, Q9, Q10, Q11]), "operationType" : NewBodyOperationType.ADD, "oppositeDirection" : true, "depth" : 15 * mm, "offsetDistance" : 25 * mm});
        }
        {
            var Q0;
            Q0=makeQuery(id+"F22.boolean.opBoolean","MERGE",FACE,{"derivedFrom":[makeQuery(id+"F15.opExtrude","CAP_FACE",FACE,{"disambiguationData":[OSD([sQuery(id+"F14.wireOp",EDGE,"E64.0"),sQuery(id+"F14.wireOp",EDGE,"E64.1"),sQuery(id+"F14.wireOp",EDGE,"E64.2"),sQuery(id+"F14.wireOp",EDGE,"E64.3")])],"isStart":false}),makeQuery(id+"F22.opExtrude","CAP_FACE",FACE,{"disambiguationData":[OSD([sQuery(id+"F21.wireOp",EDGE,"E68.bottom"),sQuery(id+"F21.wireOp",EDGE,"E68.top"),sQuery(id+"F21.wireOp",EDGE,"E68.left"),sQuery(id+"F21.wireOp",EDGE,"E68.right")])],"isStart":true}),makeQuery(id+"F22.opExtrude","CAP_FACE",FACE,{"disambiguationData":[OSD([sQuery(id+"F21.wireOp",EDGE,"E69.bottom"),sQuery(id+"F21.wireOp",EDGE,"E69.top"),sQuery(id+"F21.wireOp",EDGE,"E69.left"),sQuery(id+"F21.wireOp",EDGE,"E69.right")])],"isStart":true}),makeQuery(id+"F22.opExtrude","CAP_FACE",FACE,{"disambiguationData":[OSD([sQuery(id+"F21.wireOp",EDGE,"E70.bottom"),sQuery(id+"F21.wireOp",EDGE,"E70.top"),sQuery(id+"F21.wireOp",EDGE,"E70.left"),sQuery(id+"F21.wireOp",EDGE,"E70.right")])],"isStart":true}),makeQuery(id+"F22.opExtrude","CAP_FACE",FACE,{"disambiguationData":[OSD([sQuery(id+"F21.wireOp",EDGE,"E71.bottom"),sQuery(id+"F21.wireOp",EDGE,"E71.top"),sQuery(id+"F21.wireOp",EDGE,"E71.left"),sQuery(id+"F21.wireOp",EDGE,"E71.right")])],"isStart":true})]});
            var sketch = newSketch(context, id + "F23", { "sketchPlane" : qUnion([Q0])});
            skLineSegment(sketch, "E72.bottom", {"start": v(-45, -47.5) * mm, "end": v(45, -47.5) * mm, "construction": true});
            skLineSegment(sketch, "E72.top", {"start": v(-45, 47.5) * mm, "end": v(45, 47.5) * mm, "construction": true});
            skLineSegment(sketch, "E72.left", {"start": v(-45, -47.5) * mm, "end": v(-45, 47.5) * mm, "construction": true});
            skLineSegment(sketch, "E72.right", {"start": v(45, -47.5) * mm, "end": v(45, 47.5) * mm, "construction": true});
            skPoint(sketch, "E72.middle", {"position": v(0, 0) * mm});
            skCircle(sketch, "E73", {"center": v(-45, 47.5) * mm, "radius": 1.25 * mm});
            skCircle(sketch, "E74", {"center": v(45, 47.5) * mm, "radius": 1.25 * mm});
            skCircle(sketch, "E75", {"center": v(-45, -47.5) * mm, "radius": 1.25 * mm});
            skCircle(sketch, "E76", {"center": v(45, -47.5) * mm, "radius": 1.25 * mm});
            skSolve(sketch);
        }
        {
            var Q0;
            Q0=makeQuery(id+"F23.imprint","IMPRINT",FACE,{"disambiguationData":[TD([[makeQuery(id+"F23.imprint","IMPRINT",EDGE,{"derivedFrom":sQuery(id+"F23.wireOp",EDGE,"E73")}),1.0]])]});
            var Q1;
            Q1=makeQuery(id+"F23.imprint","IMPRINT",FACE,{"disambiguationData":[TD([[makeQuery(id+"F23.imprint","IMPRINT",EDGE,{"derivedFrom":sQuery(id+"F23.wireOp",EDGE,"E74")}),1.0]])]});
            var Q2;
            Q2=makeQuery(id+"F23.imprint","IMPRINT",FACE,{"disambiguationData":[TD([[makeQuery(id+"F23.imprint","IMPRINT",EDGE,{"derivedFrom":sQuery(id+"F23.wireOp",EDGE,"E76")}),1.0]])]});
            var Q3;
            Q3=makeQuery(id+"F23.imprint","IMPRINT",FACE,{"disambiguationData":[TD([[makeQuery(id+"F23.imprint","IMPRINT",EDGE,{"derivedFrom":sQuery(id+"F23.wireOp",EDGE,"E75")}),1.0]])]});
            extrude(context, id + "F24", {"entities" : qUnion([Q0, Q1, Q2, Q3]), "operationType" : NewBodyOperationType.REMOVE, "oppositeDirection" : true, "depth" : 10 * mm, "offsetDistance" : 25 * mm});
        }
        {
            var Q0;
            Q0=makeQuery(id+"F22.boolean.opBoolean","INTERSECT",EDGE,{"derivedFrom":[makeQuery(id+"F18.boolean.opBoolean","COPY",FACE,{"derivedFrom":makeQuery(id+"F18.opExtrude","SWEPT_FACE",FACE,{"disambiguationData":[OSD([sQuery(id+"F17.wireOp",EDGE,"E65.3")])]})}),makeQuery(id+"F22.opExtrude","SWEPT_FACE",FACE,{"disambiguationData":[OSD([sQuery(id+"F21.wireOp",EDGE,"E70.top")])]})]});
            var Q1;
            Q1=makeQuery(id+"F22.opExtrude","SWEPT_EDGE",EDGE,{"disambiguationData":[OSD([sQuery(id+"F21.wireOp",EDGE,"E70.top"),sQuery(id+"F21.wireOp",EDGE,"E70.left")])]});
            var Q2;
            Q2=makeQuery(id+"F22.boolean.opBoolean","INTERSECT",EDGE,{"derivedFrom":[makeQuery(id+"F18.boolean.opBoolean","COPY",FACE,{"derivedFrom":makeQuery(id+"F18.opExtrude","SWEPT_FACE",FACE,{"disambiguationData":[OSD([sQuery(id+"F17.wireOp",EDGE,"E65.2")])]})}),makeQuery(id+"F22.opExtrude","SWEPT_FACE",FACE,{"disambiguationData":[OSD([sQuery(id+"F21.wireOp",EDGE,"E70.left")])]})]});
            var Q3;
            Q3=makeQuery(id+"F22.boolean.opBoolean","INTERSECT",EDGE,{"derivedFrom":[makeQuery(id+"F18.boolean.opBoolean","COPY",FACE,{"derivedFrom":makeQuery(id+"F18.opExtrude","SWEPT_FACE",FACE,{"disambiguationData":[OSD([sQuery(id+"F17.wireOp",EDGE,"E65.2")])]})}),makeQuery(id+"F22.opExtrude","SWEPT_FACE",FACE,{"disambiguationData":[OSD([sQuery(id+"F21.wireOp",EDGE,"E69.right")])]})]});
            var Q4;
            Q4=makeQuery(id+"F22.opExtrude","SWEPT_EDGE",EDGE,{"disambiguationData":[OSD([sQuery(id+"F21.wireOp",EDGE,"E69.top"),sQuery(id+"F21.wireOp",EDGE,"E69.right")])]});
            var Q5;
            Q5=makeQuery(id+"F22.boolean.opBoolean","INTERSECT",EDGE,{"derivedFrom":[makeQuery(id+"F18.boolean.opBoolean","COPY",FACE,{"derivedFrom":makeQuery(id+"F18.opExtrude","SWEPT_FACE",FACE,{"disambiguationData":[OSD([sQuery(id+"F17.wireOp",EDGE,"E65.1")])]})}),makeQuery(id+"F22.opExtrude","SWEPT_FACE",FACE,{"disambiguationData":[OSD([sQuery(id+"F21.wireOp",EDGE,"E69.top")])]})]});
            var Q6;
            Q6=makeQuery(id+"F22.boolean.opBoolean","INTERSECT",EDGE,{"derivedFrom":[makeQuery(id+"F18.boolean.opBoolean","COPY",FACE,{"derivedFrom":makeQuery(id+"F18.opExtrude","SWEPT_FACE",FACE,{"disambiguationData":[OSD([sQuery(id+"F17.wireOp",EDGE,"E65.1")])]})}),makeQuery(id+"F22.opExtrude","SWEPT_FACE",FACE,{"disambiguationData":[OSD([sQuery(id+"F21.wireOp",EDGE,"E68.bottom")])]})]});
            var Q7;
            Q7=makeQuery(id+"F22.opExtrude","SWEPT_EDGE",EDGE,{"disambiguationData":[OSD([sQuery(id+"F21.wireOp",EDGE,"E68.bottom"),sQuery(id+"F21.wireOp",EDGE,"E68.left")])]});
            var Q8;
            Q8=makeQuery(id+"F22.boolean.opBoolean","INTERSECT",EDGE,{"derivedFrom":[makeQuery(id+"F18.boolean.opBoolean","COPY",FACE,{"derivedFrom":makeQuery(id+"F18.opExtrude","SWEPT_FACE",FACE,{"disambiguationData":[OSD([sQuery(id+"F17.wireOp",EDGE,"E65.0")])]})}),makeQuery(id+"F22.opExtrude","SWEPT_FACE",FACE,{"disambiguationData":[OSD([sQuery(id+"F21.wireOp",EDGE,"E68.left")])]})]});
            var Q9;
            Q9=makeQuery(id+"F22.boolean.opBoolean","INTERSECT",EDGE,{"derivedFrom":[makeQuery(id+"F18.boolean.opBoolean","COPY",FACE,{"derivedFrom":makeQuery(id+"F18.opExtrude","SWEPT_FACE",FACE,{"disambiguationData":[OSD([sQuery(id+"F17.wireOp",EDGE,"E65.3")])]})}),makeQuery(id+"F22.opExtrude","SWEPT_FACE",FACE,{"disambiguationData":[OSD([sQuery(id+"F21.wireOp",EDGE,"E71.bottom")])]})]});
            var Q10;
            Q10=makeQuery(id+"F22.opExtrude","SWEPT_EDGE",EDGE,{"disambiguationData":[OSD([sQuery(id+"F21.wireOp",EDGE,"E71.bottom"),sQuery(id+"F21.wireOp",EDGE,"E71.left")])]});
            var Q11;
            Q11=makeQuery(id+"F22.boolean.opBoolean","INTERSECT",EDGE,{"derivedFrom":[makeQuery(id+"F18.boolean.opBoolean","COPY",FACE,{"derivedFrom":makeQuery(id+"F18.opExtrude","SWEPT_FACE",FACE,{"disambiguationData":[OSD([sQuery(id+"F17.wireOp",EDGE,"E65.0")])]})}),makeQuery(id+"F22.opExtrude","SWEPT_FACE",FACE,{"disambiguationData":[OSD([sQuery(id+"F21.wireOp",EDGE,"E71.left")])]})]});
            fillet(context, id + "F25", {"entities" : qUnion([Q0, Q1, Q2, Q3, Q4, Q5, Q6, Q7, Q8, Q9, Q10, Q11]), "radius" : 1 * mm, "tangentPropagation" : true, "allowEdgeOverflow" : false});
        }
        {
            var Q0;
            Q0=makeQuery(id+"F11.boolean.opBoolean","MERGE",FACE,{"derivedFrom":[makeQuery(id+"F9.boolean.opBoolean","MERGE",FACE,{"derivedFrom":[makeQuery(id+"F7.opExtrude","SWEPT_FACE",FACE,{"disambiguationData":[OSD([sQuery(id+"F6.wireOp",EDGE,"E26.0"),sQuery(id+"F6.wireOp",EDGE,"E27"),sQuery(id+"F6.wireOp",EDGE,"E32")])]}),makeQuery(id+"F9.opExtrude","SWEPT_FACE",FACE,{"disambiguationData":[OSD([sQuery(id+"F8.wireOp",EDGE,"E47")])]})]}),makeQuery(id+"F11.opExtrude","SWEPT_FACE",FACE,{"disambiguationData":[OSD([sQuery(id+"F10.wireOp",EDGE,"E49")])]})]});
            var sketch = newSketch(context, id + "F26", { "sketchPlane" : qUnion([Q0])});
            skLineSegment(sketch, "E77.bottom", {"start": v(17.5, -66.47) * mm, "end": v(35, -66.47) * mm});
            skLineSegment(sketch, "E77.top", {"start": v(17.5, -57.97) * mm, "end": v(35, -57.97) * mm});
            skLineSegment(sketch, "E77.left", {"start": v(17.5, -66.47) * mm, "end": v(17.5, -57.97) * mm});
            skLineSegment(sketch, "E77.right", {"start": v(35, -66.47) * mm, "end": v(35, -57.97) * mm});
            skPoint(sketch, "E77.middle", {"position": v(26.25, -62.22) * mm});
            skCircle(sketch, "E78", {"center": v(37.75, -62.22) * mm, "radius": 1.5 * mm});
            skLineSegment(sketch, "E79", {"start": v(26.25, -57.97) * mm, "end": v(26.25, -62.22) * mm, "construction": true});
            skCircle(sketch, "E80.MirrorC", {"center": v(14.75, -62.22) * mm, "radius": 1.5 * mm});
            skSolve(sketch);
        }
        {
            var Q0;
            Q0 = qSketchRegion(id + "F26", true);
            extrude(context, id + "F27", {"entities" : qUnion([Q0]), "operationType" : NewBodyOperationType.REMOVE, "oppositeDirection" : true, "depth" : 25 * mm, "offsetDistance" : 25 * mm});
        }
        {
            var Q0;
            Q0=makeQuery(id+"F27.boolean.opBoolean","COPY",EDGE,{"derivedFrom":makeQuery(id+"F27.opExtrude","SWEPT_EDGE",EDGE,{"disambiguationData":[OSD([sQuery(id+"F26.wireOp",EDGE,"E77.top"),sQuery(id+"F26.wireOp",EDGE,"E77.left")])]})});
            var Q1;
            Q1=makeQuery(id+"F27.boolean.opBoolean","COPY",EDGE,{"derivedFrom":makeQuery(id+"F27.opExtrude","SWEPT_EDGE",EDGE,{"disambiguationData":[OSD([sQuery(id+"F26.wireOp",EDGE,"E77.top"),sQuery(id+"F26.wireOp",EDGE,"E77.right")])]})});
            var Q2;
            Q2=makeQuery(id+"F27.boolean.opBoolean","COPY",EDGE,{"derivedFrom":makeQuery(id+"F27.opExtrude","SWEPT_EDGE",EDGE,{"disambiguationData":[OSD([sQuery(id+"F26.wireOp",EDGE,"E77.bottom"),sQuery(id+"F26.wireOp",EDGE,"E77.left")])]})});
            var Q3;
            Q3=makeQuery(id+"F27.boolean.opBoolean","COPY",EDGE,{"derivedFrom":makeQuery(id+"F27.opExtrude","SWEPT_EDGE",EDGE,{"disambiguationData":[OSD([sQuery(id+"F26.wireOp",EDGE,"E77.bottom"),sQuery(id+"F26.wireOp",EDGE,"E77.right")])]})});
            fillet(context, id + "F28", {"entities" : qUnion([Q0, Q1, Q2, Q3]), "radius" : 1 * mm, "tangentPropagation" : true, "allowEdgeOverflow" : false});
        }
        {
            var Q0;
            {var subQ0=sQuery(id+"F0.wireOp",EDGE,"E5.MirrorC");var subQ1=sQuery(id+"F0.wireOp",EDGE,"E4.MirrorC");var subQ2=sQuery(id+"F0.wireOp",EDGE,"E3");var subQ3=sQuery(id+"F0.wireOp",EDGE,"E2");Q0=makeQuery(id+"F11.boolean.opBoolean","MERGE",FACE,{"derivedFrom":[makeQuery(id+"F9.boolean.opBoolean","MERGE",FACE,{"derivedFrom":[makeQuery(id+"F7.boolean.opBoolean","MERGE",FACE,{"derivedFrom":[makeQuery(id+"F5.boolean.opBoolean","MERGE",FACE,{"derivedFrom":[makeQuery(id+"F1.opExtrude","CAP_FACE",FACE,{"disambiguationData":[OSD([sQuery(id+"F0.wireOp",EDGE,"E0.bottom"),sQuery(id+"F0.wireOp",EDGE,"E0.top"),sQuery(id+"F0.wireOp",EDGE,"E0.left"),sQuery(id+"F0.wireOp",EDGE,"E0.right"),subQ3,subQ2,subQ1,subQ0,sQuery(id+"F0.wireOp",EDGE,"E7"),sQuery(id+"F0.wireOp",EDGE,"E8"),sQuery(id+"F0.wireOp",EDGE,"E9"),sQuery(id+"F0.wireOp",EDGE,"E10"),sQuery(id+"F0.wireOp",EDGE,"E11"),sQuery(id+"F0.wireOp",EDGE,"E12"),sQuery(id+"F0.wireOp",EDGE,"E13")])],"isStart":false}),makeQuery(id+"F5.opExtrude","CAP_FACE",FACE,{"disambiguationData":[OSD([subQ3])],"isStart":true}),makeQuery(id+"F5.opExtrude","CAP_FACE",FACE,{"disambiguationData":[OSD([subQ2])],"isStart":true}),makeQuery(id+"F5.opExtrude","CAP_FACE",FACE,{"disambiguationData":[OSD([subQ1])],"isStart":true}),makeQuery(id+"F5.opExtrude","CAP_FACE",FACE,{"disambiguationData":[OSD([subQ0])],"isStart":true})]}),makeQuery(id+"F7.opExtrude","SWEPT_FACE",FACE,{"disambiguationData":[OSD([sQuery(id+"F6.wireOp",EDGE,"E25"),sQuery(id+"F6.wireOp",EDGE,"E28")])]}),makeQuery(id+"F7.opExtrude","SWEPT_FACE",FACE,{"disambiguationData":[OSD([sQuery(id+"F6.wireOp",EDGE,"E35.MirrorCS"),sQuery(id+"F6.wireOp",EDGE,"E36.MirrorCS")])]})]}),makeQuery(id+"F9.opExtrude","SWEPT_FACE",FACE,{"disambiguationData":[OSD([sQuery(id+"F8.wireOp",EDGE,"E46")])]})]}),makeQuery(id+"F11.opExtrude","SWEPT_FACE",FACE,{"disambiguationData":[OSD([sQuery(id+"F10.wireOp",EDGE,"E50")])]})]});}
            var sketch = newSketch(context, id + "F29", { "sketchPlane" : qUnion([Q0])});
            skCircle(sketch, "E81", {"center": v(24.5, -2.5) * mm, "radius": 12.1 * mm});
            skCircle(sketch, "E82", {"center": v(14, 8) * mm, "radius": 3.5 * mm});
            skCircle(sketch, "E83", {"center": v(14, -13) * mm, "radius": 3.5 * mm});
            skCircle(sketch, "E84", {"center": v(35, -13) * mm, "radius": 3.5 * mm});
            skCircle(sketch, "E85", {"center": v(35, 8) * mm, "radius": 3.5 * mm});
            skSolve(sketch);
        }
        {
            var Q0;
            {var subQ0=sQuery(id+"F0.wireOp",EDGE,"E12");Q0=makeQuery(id+"F29.imprint","IMPRINT",FACE,{"disambiguationData":[TD([[makeQuery(id+"F29.imprint","IMPRINT",EDGE,{"derivedFrom":makeQuery(id+"F1.opExtrude","CAP_EDGE",EDGE,{"disambiguationData":[OSD([subQ0])],"isStart":false})}),-1.0]])]});}
            var Q1;
            Q1=makeQuery(id+"F29.imprint","IMPRINT",FACE,{"disambiguationData":[TD([[makeQuery(id+"F29.imprint","IMPRINT",EDGE,{"derivedFrom":makeQuery(id+"F1.opExtrude","CAP_EDGE",EDGE,{"disambiguationData":[OSD([sQuery(id+"F0.wireOp",EDGE,"E7")])],"isStart":false})}),-1.0]])]});
            var Q2;
            Q2=makeQuery(id+"F29.imprint","IMPRINT",FACE,{"disambiguationData":[TD([[makeQuery(id+"F29.imprint","IMPRINT",EDGE,{"derivedFrom":makeQuery(id+"F1.opExtrude","CAP_EDGE",EDGE,{"disambiguationData":[OSD([sQuery(id+"F0.wireOp",EDGE,"E8")])],"isStart":false})}),-1.0]])]});
            var Q3;
            Q3=makeQuery(id+"F29.imprint","IMPRINT",FACE,{"disambiguationData":[TD([[makeQuery(id+"F29.imprint","IMPRINT",EDGE,{"derivedFrom":makeQuery(id+"F1.opExtrude","CAP_EDGE",EDGE,{"disambiguationData":[OSD([sQuery(id+"F0.wireOp",EDGE,"E10")])],"isStart":false})}),-1.0]])]});
            var Q4;
            Q4=makeQuery(id+"F29.imprint","IMPRINT",FACE,{"disambiguationData":[TD([[makeQuery(id+"F29.imprint","IMPRINT",EDGE,{"derivedFrom":makeQuery(id+"F1.opExtrude","CAP_EDGE",EDGE,{"disambiguationData":[OSD([sQuery(id+"F0.wireOp",EDGE,"E9")])],"isStart":false})}),-1.0]])]});
            var Q5;
            Q5=makeQuery(id+"F29.imprint","IMPRINT",FACE,{"disambiguationData":[TD([[makeQuery(id+"F29.imprint","IMPRINT",EDGE,{"derivedFrom":makeQuery(id+"F1.opExtrude","CAP_EDGE",EDGE,{"disambiguationData":[OSD([sQuery(id+"F0.wireOp",EDGE,"E11")])],"isStart":false})}),-1.0]])]});
            var Q6;
            {var subQ0=sQuery(id+"F29.wireOp",EDGE,"E85");var subQ1=sQuery(id+"F29.wireOp",EDGE,"E81");var subQ2=makeQuery(id+"F29.imprint","INTERSECT",VERTEX,{"disambiguationData":[OD(0.0)],"derivedFrom":[subQ1,subQ0]});Q6=makeQuery(id+"F29.imprint","IMPRINT",FACE,{"disambiguationData":[TD([[makeQuery(id+"F29.imprint","IMPRINT",EDGE,{"disambiguationData":[TD([[subQ2,1.0]])],"derivedFrom":subQ1}),1.0]])]});}
            var Q7;
            {var subQ0=sQuery(id+"F29.wireOp",EDGE,"E82");var subQ1=sQuery(id+"F29.wireOp",EDGE,"E81");var subQ2=makeQuery(id+"F29.imprint","INTERSECT",VERTEX,{"disambiguationData":[OD(0.0)],"derivedFrom":[subQ1,subQ0]});Q7=makeQuery(id+"F29.imprint","IMPRINT",FACE,{"disambiguationData":[TD([[makeQuery(id+"F29.imprint","IMPRINT",EDGE,{"disambiguationData":[TD([[subQ2,-1.0]])],"derivedFrom":subQ1}),1.0]])]});}
            var Q8;
            {var subQ0=sQuery(id+"F29.wireOp",EDGE,"E83");var subQ1=sQuery(id+"F29.wireOp",EDGE,"E81");var subQ2=makeQuery(id+"F29.imprint","INTERSECT",VERTEX,{"disambiguationData":[OD(0.0)],"derivedFrom":[subQ1,subQ0]});Q8=makeQuery(id+"F29.imprint","IMPRINT",FACE,{"disambiguationData":[TD([[makeQuery(id+"F29.imprint","IMPRINT",EDGE,{"disambiguationData":[TD([[subQ2,-1.0]])],"derivedFrom":subQ1}),1.0]])]});}
            var Q9;
            {var subQ0=sQuery(id+"F29.wireOp",EDGE,"E84");var subQ1=sQuery(id+"F29.wireOp",EDGE,"E81");var subQ2=makeQuery(id+"F29.imprint","INTERSECT",VERTEX,{"disambiguationData":[OD(0.0)],"derivedFrom":[subQ1,subQ0]});Q9=makeQuery(id+"F29.imprint","IMPRINT",FACE,{"disambiguationData":[TD([[makeQuery(id+"F29.imprint","IMPRINT",EDGE,{"disambiguationData":[TD([[subQ2,-1.0]])],"derivedFrom":subQ1}),1.0]])]});}
            extrude(context, id + "F30", {"entities" : qUnion([Q0, Q1, Q2, Q3, Q4, Q5, Q6, Q7, Q8, Q9]), "depth" : 2 * mm, "offsetDistance" : 25 * mm});
        }
        {
            var Q0;
            Q0=makeQuery(id+"F5.opExtrude","CAP_FACE",FACE,{"disambiguationData":[OSD([sQuery(id+"F0.wireOp",EDGE,"E5.MirrorC")])],"isStart":false});
            var Q1;
            Q1=makeQuery(id+"F5.opExtrude","CAP_FACE",FACE,{"disambiguationData":[OSD([sQuery(id+"F0.wireOp",EDGE,"E4.MirrorC")])],"isStart":false});
            var Q2;
            Q2=makeQuery(id+"F5.opExtrude","CAP_FACE",FACE,{"disambiguationData":[OSD([sQuery(id+"F0.wireOp",EDGE,"E3")])],"isStart":false});
            var Q3;
            Q3=makeQuery(id+"F5.opExtrude","CAP_FACE",FACE,{"disambiguationData":[OSD([sQuery(id+"F0.wireOp",EDGE,"E2")])],"isStart":false});
            extrude(context, id + "F31", {"entities" : qUnion([Q0, Q1, Q2, Q3]), "operationType" : NewBodyOperationType.REMOVE, "oppositeDirection" : true, "depth" : 50 * mm, "offsetDistance" : 25 * mm});
        }
    });
